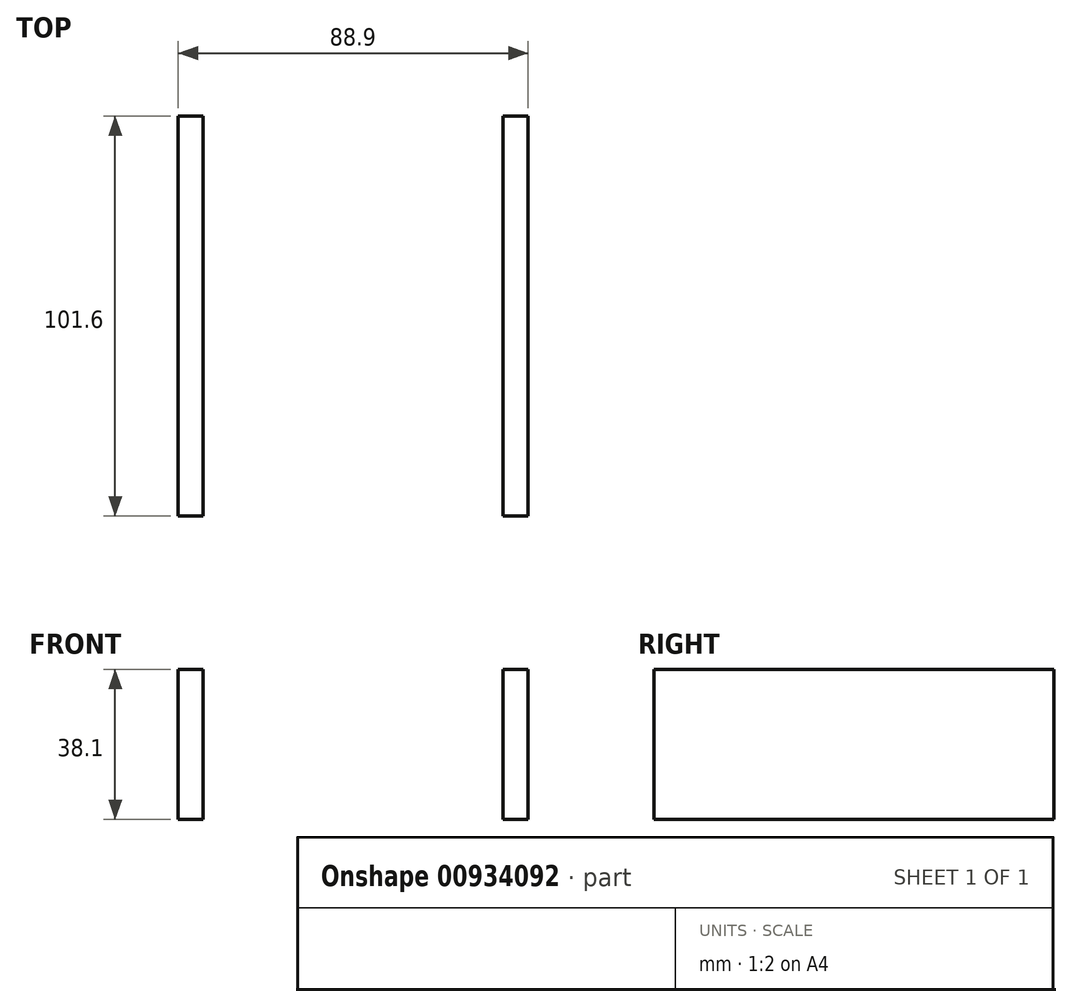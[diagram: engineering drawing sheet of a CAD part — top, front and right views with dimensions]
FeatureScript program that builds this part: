
annotation { "Feature Type Name" : "Feature", "Feature Type Description" : "" }
export const myFeature = defineFeature(function(context is Context, id is Id, definition is map)
    precondition{}
    {
        {
            var Q0;
            Q0=qCreatedBy(makeId("Right.planeOp"),FACE);
            cPlane(context, id + "F0", {"entities" : qUnion([Q0]), "cplaneType" : CPlaneType.OFFSET, "offset" : 38.1 * mm, "width" : 152.4 * mm, "height" : 152.4 * mm});
        }
        {
            var Q0;
            Q0=qCreatedBy(makeId("Right.planeOp"),FACE);
            cPlane(context, id + "F1", {"entities" : qUnion([Q0]), "cplaneType" : CPlaneType.OFFSET, "offset" : 38.1 * mm, "oppositeDirection" : true, "width" : 152.4 * mm, "height" : 152.4 * mm});
        }
        {
            var Q0;
            Q0=qCreatedBy(id+"F1.planeOp",FACE);
            var sketch = newSketch(context, id + "F2", { "sketchPlane" : qUnion([Q0])});
            skLineSegment(sketch, "E0.bottom", {"start": v(50.8, 19.05) * mm, "end": v(-50.8, 19.05) * mm});
            skLineSegment(sketch, "E0.top", {"start": v(50.8, -19.05) * mm, "end": v(-50.8, -19.05) * mm});
            skLineSegment(sketch, "E0.left", {"start": v(50.8, 19.05) * mm, "end": v(50.8, -19.05) * mm});
            skLineSegment(sketch, "E0.right", {"start": v(-50.8, 19.05) * mm, "end": v(-50.8, -19.05) * mm});
            skPoint(sketch, "E0.middle", {"position": v(0, 0) * mm});
            skSolve(sketch);
        }
        {
            var Q0;
            Q0=qCreatedBy(id+"F0.planeOp",FACE);
            var sketch = newSketch(context, id + "F3", { "sketchPlane" : qUnion([Q0])});
            skLineSegment(sketch, "E1.bottom", {"start": v(50.8, 19.05) * mm, "end": v(-50.8, 19.05) * mm});
            skLineSegment(sketch, "E1.top", {"start": v(50.8, -19.05) * mm, "end": v(-50.8, -19.05) * mm});
            skLineSegment(sketch, "E1.left", {"start": v(50.8, 19.05) * mm, "end": v(50.8, -19.05) * mm});
            skLineSegment(sketch, "E1.right", {"start": v(-50.8, 19.05) * mm, "end": v(-50.8, -19.05) * mm});
            skPoint(sketch, "E1.middle", {"position": v(0, 0) * mm});
            skSolve(sketch);
        }
        {
            var Q0;
            Q0=makeQuery(id+"F3.imprint","IMPRINT",FACE,{"disambiguationData":[TD([[makeQuery(id+"F3.imprint","IMPRINT",EDGE,{"derivedFrom":sQuery(id+"F3.wireOp",EDGE,"E1.bottom")}),1.0]])]});
            extrude(context, id + "F4", {"entities" : qUnion([Q0]), "depth" : 6.35 * mm, "offsetDistance" : 25.4 * mm});
        }
        {
            var Q0;
            Q0=makeQuery(id+"F2.imprint","IMPRINT",FACE,{"disambiguationData":[TD([[makeQuery(id+"F2.imprint","IMPRINT",EDGE,{"derivedFrom":sQuery(id+"F2.wireOp",EDGE,"E0.bottom")}),1.0]])]});
            extrude(context, id + "F5", {"entities" : qUnion([Q0]), "oppositeDirection" : true, "depth" : 6.35 * mm, "offsetDistance" : 25.4 * mm});
        }
    });
